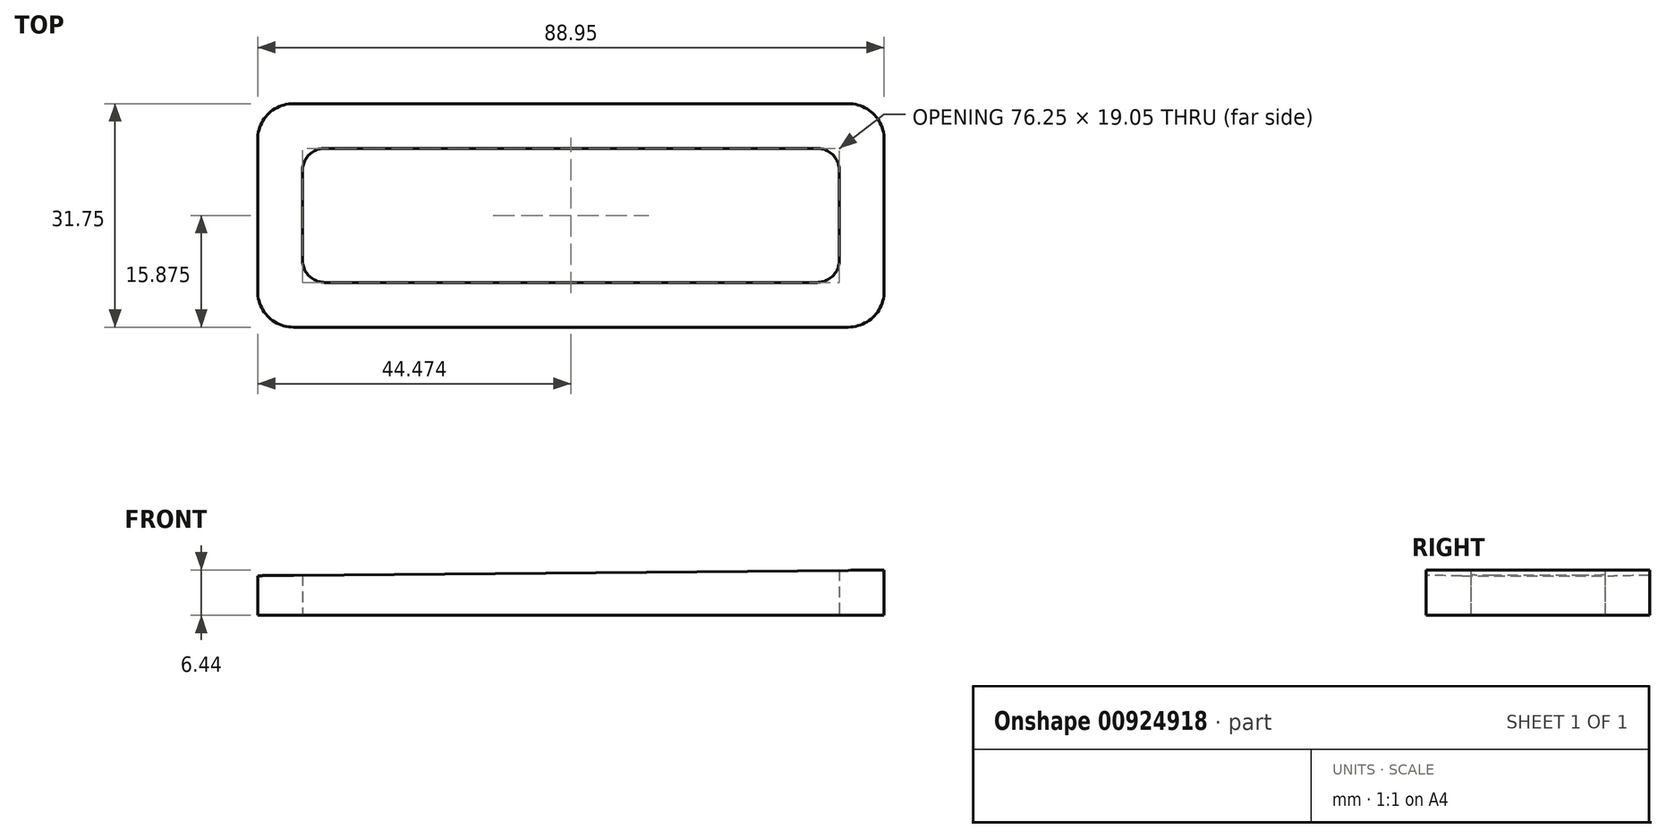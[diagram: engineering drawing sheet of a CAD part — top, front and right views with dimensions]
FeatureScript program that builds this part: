
annotation { "Feature Type Name" : "Feature", "Feature Type Description" : "" }
export const myFeature = defineFeature(function(context is Context, id is Id, definition is map)
    precondition{}
    {
        {
            var Q0;
            Q0=qCreatedBy(makeId("Front.planeOp"),FACE);
            var sketch = newSketch(context, id + "F0", { "sketchPlane" : qUnion([Q0])});
            skLineSegment(sketch, "E0", {"start": v(0, 0) * mm, "end": v(0, 2.39) * mm});
            skLineSegment(sketch, "E1", {"start": v(0, 2.39) * mm, "end": v(609.6, 7.95) * mm});
            skLineSegment(sketch, "E2", {"start": v(609.6, 7.95) * mm, "end": v(609.6, 0) * mm});
            skLineSegment(sketch, "E3", {"start": v(609.6, 0) * mm, "end": v(0, 0) * mm});
            skSolve(sketch);
        }
        {
            var Q0;
            Q0=qCreatedBy(makeId("Front.planeOp"),FACE);
            var sketch = newSketch(context, id + "F1", { "sketchPlane" : qUnion([Q0])});
            skLineSegment(sketch, "E4", {"start": v(609.6, 7.95) * mm, "end": v(520.7, 7.14) * mm});
            skLineSegment(sketch, "E5", {"start": v(520.7, 7.14) * mm, "end": v(520.7, 0) * mm});
            skLineSegment(sketch, "E6", {"start": v(520.7, 0) * mm, "end": v(609.6, 0) * mm});
            skLineSegment(sketch, "E7", {"start": v(609.6, 0) * mm, "end": v(609.6, 7.95) * mm});
            skSolve(sketch);
        }
        {
            var Q0;
            Q0=qCreatedBy(makeId("Front.planeOp"),FACE);
            var sketch = newSketch(context, id + "F2", { "sketchPlane" : qUnion([Q0])});
            skLineSegment(sketch, "E8", {"start": v(444.5, 6.44) * mm, "end": v(444.5, 0) * mm});
            skLineSegment(sketch, "E9", {"start": v(444.5, 0) * mm, "end": v(355.6, 0) * mm});
            skLineSegment(sketch, "E10", {"start": v(-261.65, 0) * mm, "end": v(-261.65, 0) * mm});
            skLineSegment(sketch, "E11", {"start": v(355.55, 5.63) * mm, "end": v(444.5, 6.44) * mm});
            skLineSegment(sketch, "E12", {"start": v(355.55, 5.63) * mm, "end": v(355.6, 0) * mm});
            skSolve(sketch);
        }
        {
            var Q0;
            Q0=qSketchRegion(id+"F2",true);
            extrude(context, id + "F3", {"entities" : qUnion([Q0]), "depth" : 31.75 * mm, "offsetDistance" : 25.4 * mm});
        }
        {
            var Q0;
            Q0=makeQuery(id+"F3.opExtrude","SWEPT_FACE",FACE,{"disambiguationData":[OSD([sQuery(id+"F2.wireOp",EDGE,"E9")])]});
            var sketch = newSketch(context, id + "F4", { "sketchPlane" : qUnion([Q0])});
            skLineSegment(sketch, "E13.bottom", {"start": v(365.07, 25.4) * mm, "end": v(434.98, 25.4) * mm});
            skLineSegment(sketch, "E13.top", {"start": v(365.07, 6.35) * mm, "end": v(434.98, 6.35) * mm});
            skLineSegment(sketch, "E13.left", {"start": v(361.9, 22.22) * mm, "end": v(361.9, 9.52) * mm});
            skLineSegment(sketch, "E13.right", {"start": v(438.15, 22.23) * mm, "end": v(438.15, 9.53) * mm});
            skPoint(sketch, "E14.visualSharp", {"position": v(361.9, 25.4) * mm});
            skArc(sketch, "E14.filletArc", {"start": v(365.07, 25.4) * mm, "mid": v(362.83, 24.47) * mm, "end": v(361.9, 22.22) * mm});
            skPoint(sketch, "E15.visualSharp", {"position": v(438.15, 25.4) * mm});
            skArc(sketch, "E15.filletArc", {"start": v(438.15, 22.23) * mm, "mid": v(437.22, 24.47) * mm, "end": v(434.98, 25.4) * mm});
            skPoint(sketch, "E16.visualSharp", {"position": v(438.15, 6.35) * mm});
            skArc(sketch, "E16.filletArc", {"start": v(434.98, 6.35) * mm, "mid": v(437.22, 7.28) * mm, "end": v(438.15, 9.53) * mm});
            skPoint(sketch, "E17.visualSharp", {"position": v(361.9, 6.35) * mm});
            skArc(sketch, "E17.filletArc", {"start": v(361.9, 9.52) * mm, "mid": v(362.83, 7.28) * mm, "end": v(365.07, 6.35) * mm});
            skSolve(sketch);
        }
        {
            var Q0;
            Q0=makeQuery(id+"F4.imprint","IMPRINT",FACE,{"disambiguationData":[TD([[makeQuery(id+"F4.imprint","IMPRINT",EDGE,{"derivedFrom":sQuery(id+"F4.wireOp",EDGE,"E13.bottom")}),-1.0]])]});
            extrude(context, id + "F5", {"entities" : qUnion([Q0]), "operationType" : NewBodyOperationType.REMOVE, "endBound" : BoundingType.THROUGH_ALL, "oppositeDirection" : true, "depth" : 25.4 * mm, "offsetDistance" : 25.4 * mm});
        }
        {
            var Q0;
            Q0=makeQuery(id+"F3.opExtrude","CAP_EDGE",EDGE,{"disambiguationData":[OSD([sQuery(id+"F2.wireOp",EDGE,"E8")])],"isStart":false});
            var Q1;
            Q1=makeQuery(id+"F3.opExtrude","CAP_EDGE",EDGE,{"disambiguationData":[OSD([sQuery(id+"F2.wireOp",EDGE,"E12")])],"isStart":false});
            var Q2;
            Q2=makeQuery(id+"F3.opExtrude","CAP_EDGE",EDGE,{"disambiguationData":[OSD([sQuery(id+"F2.wireOp",EDGE,"E12")])],"isStart":true});
            var Q3;
            Q3=makeQuery(id+"F3.opExtrude","CAP_EDGE",EDGE,{"disambiguationData":[OSD([sQuery(id+"F2.wireOp",EDGE,"E8")])],"isStart":true});
            fillet(context, id + "F6", {"entities" : qUnion([Q0, Q1, Q2, Q3]), "radius" : 5.08 * mm, "tangentPropagation" : true, "allowEdgeOverflow" : false});
        }
    });
